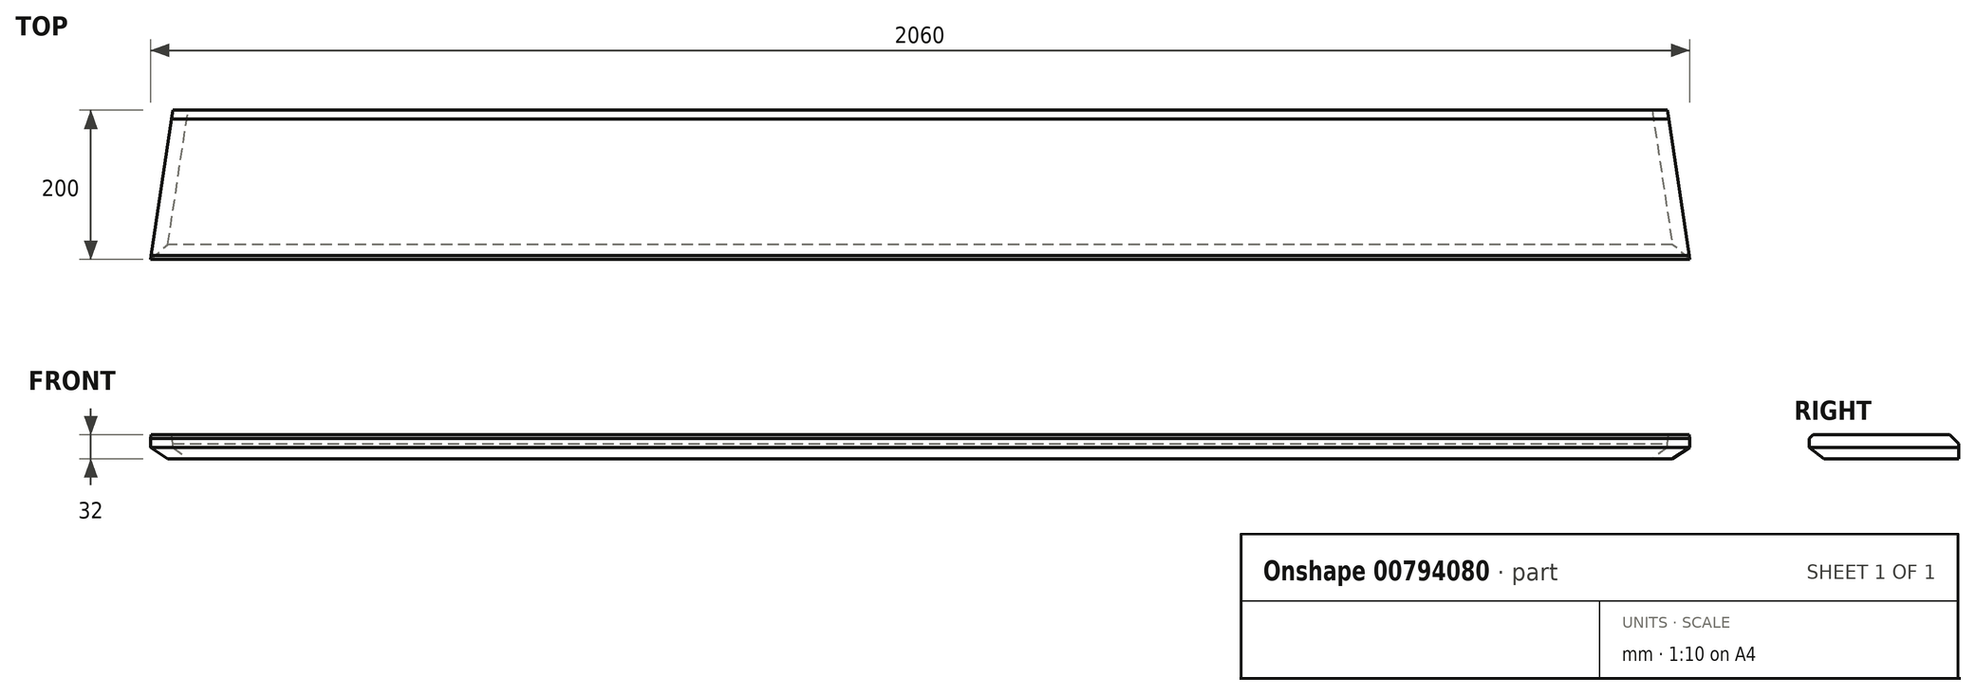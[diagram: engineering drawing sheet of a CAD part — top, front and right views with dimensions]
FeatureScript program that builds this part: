
annotation { "Feature Type Name" : "Feature", "Feature Type Description" : "" }
export const myFeature = defineFeature(function(context is Context, id is Id, definition is map)
    precondition{}
    {
        {
            var Q0;
            Q0=qCreatedBy(makeId("Front.planeOp"),FACE);
            var sketch = newSketch(context, id + "F0", { "sketchPlane" : qUnion([Q0])});
            skLineSegment(sketch, "E0.bottom", {"start": v(0, 0) * mm, "end": v(-2000, 0) * mm});
            skLineSegment(sketch, "E0.top", {"start": v(0, 32) * mm, "end": v(-2000, 32) * mm});
            skLineSegment(sketch, "E0.left", {"start": v(0, 0) * mm, "end": v(0, 32) * mm});
            skLineSegment(sketch, "E0.right", {"start": v(-2000, 0) * mm, "end": v(-2000, 32) * mm});
            skSolve(sketch);
        }
        {
            var Q0;
            Q0 = qSketchRegion(id + "F0", true);
            extrude(context, id + "F1", {"entities" : qUnion([Q0]), "depth" : 200 * mm, "offsetDistance" : 25 * mm});
        }
        {
            var Q0;
            Q0=makeQuery(id+"F1.opExtrude","CAP_EDGE",EDGE,{"disambiguationData":[OSD([sQuery(id+"F0.wireOp",EDGE,"E0.top")])],"isStart":true});
            chamfer(context, id + "F2", {"entities" : qUnion([Q0]), "width" : 12 * mm, "tangentPropagation" : true});
        }
        {
            var Q0;
            Q0=makeQuery(id+"F1.opExtrude","CAP_EDGE",EDGE,{"disambiguationData":[OSD([sQuery(id+"F0.wireOp",EDGE,"E0.top")])],"isStart":false});
            chamfer(context, id + "F3", {"entities" : qUnion([Q0]), "width" : 5 * mm, "tangentPropagation" : true});
        }
        {
            var Q0;
            Q0=qCreatedBy(makeId("Top.planeOp"),FACE);
            var sketch = newSketch(context, id + "F4", { "sketchPlane" : qUnion([Q0])});
            skLineSegment(sketch, "E1", {"start": v(0, 0) * mm, "end": v(0, -200) * mm});
            skLineSegment(sketch, "E2", {"start": v(0, -200) * mm, "end": v(30, -200) * mm});
            skLineSegment(sketch, "E3", {"start": v(30, -200) * mm, "end": v(0, 0) * mm});
            skLineSegment(sketch, "E4", {"start": v(0, 0) * mm, "end": v(-1000, 0) * mm, "construction": true});
            skLineSegment(sketch, "E5", {"start": v(-1000, 0) * mm, "end": v(-1000, -68.7) * mm, "construction": true});
            skLineSegment(sketch, "E6.MirrorCS", {"start": v(-2030, -200) * mm, "end": v(-2000, 0) * mm});
            skLineSegment(sketch, "E7.MirrorCS", {"start": v(-2000, 0) * mm, "end": v(-2000, -200) * mm});
            skLineSegment(sketch, "E8.MirrorCS", {"start": v(-2000, -200) * mm, "end": v(-2030, -200) * mm});
            skSolve(sketch);
        }
        {
            var Q0;
            Q0 = qSketchRegion(id + "F4", true);
            extrude(context, id + "F5", {"entities" : qUnion([Q0]), "operationType" : NewBodyOperationType.ADD, "depth" : 32 * mm, "offsetDistance" : 25 * mm});
        }
        {
            var Q0;
            Q0=makeQuery(id+"F5.opExtrude","CAP_EDGE",EDGE,{"disambiguationData":[OSD([sQuery(id+"F4.wireOp",EDGE,"E8.MirrorCS")])],"isStart":false});
            chamfer(context, id + "F6", {"entities" : qUnion([Q0]), "width" : 5 * mm, "tangentPropagation" : true});
        }
        {
            var Q0;
            Q0=makeQuery(id+"F5.opExtrude","CAP_EDGE",EDGE,{"disambiguationData":[OSD([sQuery(id+"F4.wireOp",EDGE,"E2")])],"isStart":false});
            chamfer(context, id + "F7", {"entities" : qUnion([Q0]), "width" : 5 * mm, "tangentPropagation" : true});
        }
        {
            var Q0;
            Q0=qCreatedBy(makeId("Right.planeOp"),FACE);
            var sketch = newSketch(context, id + "F8", { "sketchPlane" : qUnion([Q0])});
            skLineSegment(sketch, "E9", {"start": v(0, 20) * mm, "end": v(0, 32) * mm});
            skLineSegment(sketch, "E10", {"start": v(0, 32) * mm, "end": v(-12, 32) * mm});
            skLineSegment(sketch, "E11", {"start": v(-12, 32) * mm, "end": v(0, 20) * mm});
            skSolve(sketch);
        }
        {
            var Q0;
            Q0 = qSketchRegion(id + "F8", true);
            extrude(context, id + "F9", {"entities" : qUnion([Q0]), "operationType" : NewBodyOperationType.REMOVE, "endBound" : BoundingType.SYMMETRIC, "oppositeDirection" : true, "depth" : 4194 * mm, "offsetDistance" : 25 * mm});
        }
        {
            var Q0;
            Q0=makeQuery(id+"F5.boolean.opBoolean","MERGE",EDGE,{"derivedFrom":[makeQuery(id+"F1.opExtrude","CAP_EDGE",EDGE,{"disambiguationData":[OSD([sQuery(id+"F0.wireOp",EDGE,"E0.bottom")])],"isStart":false}),makeQuery(id+"F5.opExtrude","CAP_EDGE",EDGE,{"disambiguationData":[OSD([sQuery(id+"F4.wireOp",EDGE,"E2")])],"isStart":true}),makeQuery(id+"F5.opExtrude","CAP_EDGE",EDGE,{"disambiguationData":[OSD([sQuery(id+"F4.wireOp",EDGE,"E8.MirrorCS")])],"isStart":true})]});
            var Q1;
            Q1=makeQuery(id+"F5.opExtrude","CAP_EDGE",EDGE,{"disambiguationData":[OSD([sQuery(id+"F4.wireOp",EDGE,"E6.MirrorCS")])],"isStart":true});
            var Q2;
            Q2=makeQuery(id+"F5.opExtrude","CAP_EDGE",EDGE,{"disambiguationData":[OSD([sQuery(id+"F4.wireOp",EDGE,"E3")])],"isStart":true});
            chamfer(context, id + "F10", {"entities" : qUnion([Q0, Q1, Q2]), "chamferType" : ChamferType.TWO_OFFSETS, "width1" : 20 * mm, "oppositeDirection" : false, "width2" : 15 * mm, "tangentPropagation" : true});
        }
    });
